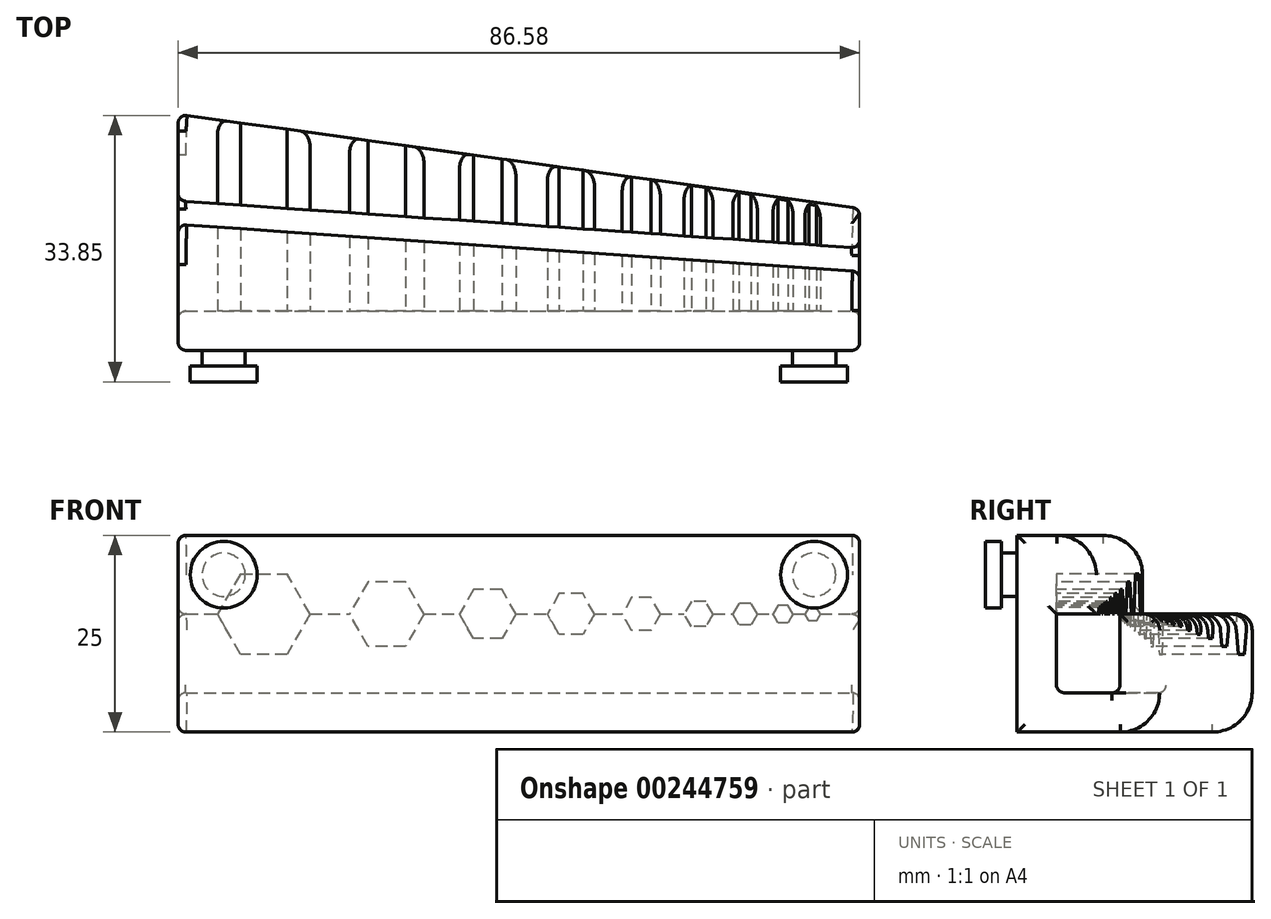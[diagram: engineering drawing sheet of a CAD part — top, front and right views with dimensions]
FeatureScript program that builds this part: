
annotation { "Feature Type Name" : "Feature", "Feature Type Description" : "" }
export const myFeature = defineFeature(function(context is Context, id is Id, definition is map)
    precondition{}
    {
        {
            var Q0;
            Q0=qCreatedBy(makeId("Front.planeOp"),FACE);
            var sketch = newSketch(context, id + "F0", { "sketchPlane" : qUnion([Q0])});
            skCircle(sketch, "E0.cCircle", {"center": v(-32.4, 0) * mm, "radius": 5.1 * mm, "construction": true});
            skLineSegment(sketch, "E0.0", {"start": v(-35.34, 5.1) * mm, "end": v(-29.45, 5.1) * mm});
            skLineSegment(sketch, "E0.1", {"start": v(-29.45, 5.1) * mm, "end": v(-26.5, 0) * mm});
            skLineSegment(sketch, "E0.2", {"start": v(-26.5, 0) * mm, "end": v(-29.45, -5.1) * mm});
            skLineSegment(sketch, "E0.3", {"start": v(-29.45, -5.1) * mm, "end": v(-35.34, -5.1) * mm});
            skLineSegment(sketch, "E0.4", {"start": v(-35.34, -5.1) * mm, "end": v(-38.29, 0) * mm});
            skLineSegment(sketch, "E0.5", {"start": v(-38.29, 0) * mm, "end": v(-35.34, 5.1) * mm});
            skPoint(sketch, "E0.0.midPoint", {"position": v(-32.4, 5.1) * mm});
            skCircle(sketch, "E1.cCircle", {"center": v(-16.78, 0) * mm, "radius": 4.1 * mm, "construction": true});
            skLineSegment(sketch, "E1.0", {"start": v(-14.4, -4.1) * mm, "end": v(-19.14, -4.1) * mm});
            skLineSegment(sketch, "E1.1", {"start": v(-19.14, -4.1) * mm, "end": v(-21.5, 0) * mm});
            skLineSegment(sketch, "E1.2", {"start": v(-21.5, 0) * mm, "end": v(-19.14, 4.1) * mm});
            skLineSegment(sketch, "E1.3", {"start": v(-19.14, 4.1) * mm, "end": v(-14.4, 4.1) * mm});
            skLineSegment(sketch, "E1.4", {"start": v(-14.4, 4.1) * mm, "end": v(-12.04, 0) * mm});
            skLineSegment(sketch, "E1.5", {"start": v(-12.04, 0) * mm, "end": v(-14.4, -4.1) * mm});
            skPoint(sketch, "E1.0.midPoint", {"position": v(-16.78, -4.1) * mm});
            skCircle(sketch, "E2.cCircle", {"center": v(-3.96, 0) * mm, "radius": 3.1 * mm, "construction": true});
            skLineSegment(sketch, "E2.0", {"start": v(-2.17, -3.1) * mm, "end": v(-5.75, -3.1) * mm});
            skLineSegment(sketch, "E2.1", {"start": v(-5.75, -3.1) * mm, "end": v(-7.54, 0) * mm});
            skLineSegment(sketch, "E2.2", {"start": v(-7.54, 0) * mm, "end": v(-5.75, 3.1) * mm});
            skLineSegment(sketch, "E2.3", {"start": v(-5.75, 3.1) * mm, "end": v(-2.17, 3.1) * mm});
            skLineSegment(sketch, "E2.4", {"start": v(-2.17, 3.1) * mm, "end": v(-0.38, 0) * mm});
            skLineSegment(sketch, "E2.5", {"start": v(-0.38, 0) * mm, "end": v(-2.17, -3.1) * mm});
            skPoint(sketch, "E2.0.midPoint", {"position": v(-3.96, -3.1) * mm});
            skCircle(sketch, "E3.cCircle", {"center": v(6.62, 0) * mm, "radius": 2.6 * mm, "construction": true});
            skLineSegment(sketch, "E3.0", {"start": v(8.12, -2.6) * mm, "end": v(5.12, -2.6) * mm});
            skLineSegment(sketch, "E3.1", {"start": v(5.12, -2.6) * mm, "end": v(3.62, 0) * mm});
            skLineSegment(sketch, "E3.2", {"start": v(3.62, 0) * mm, "end": v(5.12, 2.6) * mm});
            skLineSegment(sketch, "E3.3", {"start": v(5.12, 2.6) * mm, "end": v(8.12, 2.6) * mm});
            skLineSegment(sketch, "E3.4", {"start": v(8.12, 2.6) * mm, "end": v(9.62, 0) * mm});
            skLineSegment(sketch, "E3.5", {"start": v(9.62, 0) * mm, "end": v(8.12, -2.6) * mm});
            skPoint(sketch, "E3.0.midPoint", {"position": v(6.62, -2.6) * mm});
            skCircle(sketch, "E4.cCircle", {"center": v(15.55, 0) * mm, "radius": 2.1 * mm, "construction": true});
            skLineSegment(sketch, "E4.0", {"start": v(16.76, -2.1) * mm, "end": v(14.33, -2.1) * mm});
            skLineSegment(sketch, "E4.1", {"start": v(14.33, -2.1) * mm, "end": v(13.12, 0) * mm});
            skLineSegment(sketch, "E4.2", {"start": v(13.12, 0) * mm, "end": v(14.33, 2.1) * mm});
            skLineSegment(sketch, "E4.3", {"start": v(14.33, 2.1) * mm, "end": v(16.76, 2.1) * mm});
            skLineSegment(sketch, "E4.4", {"start": v(16.76, 2.1) * mm, "end": v(17.97, 0) * mm});
            skLineSegment(sketch, "E4.5", {"start": v(17.97, 0) * mm, "end": v(16.76, -2.1) * mm});
            skPoint(sketch, "E4.0.midPoint", {"position": v(15.55, -2.1) * mm});
            skCircle(sketch, "E5.cCircle", {"center": v(22.82, 0) * mm, "radius": 1.6 * mm, "construction": true});
            skLineSegment(sketch, "E5.0", {"start": v(23.74, -1.6) * mm, "end": v(21.9, -1.6) * mm});
            skLineSegment(sketch, "E5.1", {"start": v(21.9, -1.6) * mm, "end": v(20.97, 0) * mm});
            skLineSegment(sketch, "E5.2", {"start": v(20.97, 0) * mm, "end": v(21.9, 1.6) * mm});
            skLineSegment(sketch, "E5.3", {"start": v(21.9, 1.6) * mm, "end": v(23.74, 1.6) * mm});
            skLineSegment(sketch, "E5.4", {"start": v(23.74, 1.6) * mm, "end": v(24.67, 0) * mm});
            skLineSegment(sketch, "E5.5", {"start": v(24.67, 0) * mm, "end": v(23.74, -1.6) * mm});
            skPoint(sketch, "E5.0.midPoint", {"position": v(22.82, -1.6) * mm});
            skCircle(sketch, "E6.cCircle", {"center": v(28.73, 0) * mm, "radius": 1.35 * mm, "construction": true});
            skLineSegment(sketch, "E6.0", {"start": v(29.5, -1.35) * mm, "end": v(27.95, -1.35) * mm});
            skLineSegment(sketch, "E6.1", {"start": v(27.95, -1.35) * mm, "end": v(27.17, 0) * mm});
            skLineSegment(sketch, "E6.2", {"start": v(27.17, 0) * mm, "end": v(27.95, 1.35) * mm});
            skLineSegment(sketch, "E6.3", {"start": v(27.95, 1.35) * mm, "end": v(29.5, 1.35) * mm});
            skLineSegment(sketch, "E6.4", {"start": v(29.5, 1.35) * mm, "end": v(30.28, 0) * mm});
            skLineSegment(sketch, "E6.5", {"start": v(30.28, 0) * mm, "end": v(29.5, -1.35) * mm});
            skPoint(sketch, "E6.0.midPoint", {"position": v(28.73, -1.35) * mm});
            skCircle(sketch, "E7.cCircle", {"center": v(33.55, 0) * mm, "radius": 1.1 * mm, "construction": true});
            skLineSegment(sketch, "E7.0", {"start": v(34.19, -1.1) * mm, "end": v(32.92, -1.1) * mm});
            skLineSegment(sketch, "E7.1", {"start": v(32.92, -1.1) * mm, "end": v(32.28, 0) * mm});
            skLineSegment(sketch, "E7.2", {"start": v(32.28, 0) * mm, "end": v(32.92, 1.1) * mm});
            skLineSegment(sketch, "E7.3", {"start": v(32.92, 1.1) * mm, "end": v(34.19, 1.1) * mm});
            skLineSegment(sketch, "E7.4", {"start": v(34.19, 1.1) * mm, "end": v(34.82, 0) * mm});
            skLineSegment(sketch, "E7.5", {"start": v(34.82, 0) * mm, "end": v(34.19, -1.1) * mm});
            skPoint(sketch, "E7.0.midPoint", {"position": v(33.55, -1.1) * mm});
            skCircle(sketch, "E8.cCircle", {"center": v(37.3, 0) * mm, "radius": 0.85 * mm, "construction": true});
            skLineSegment(sketch, "E8.0", {"start": v(37.8, -0.85) * mm, "end": v(36.82, -0.85) * mm});
            skLineSegment(sketch, "E8.1", {"start": v(36.82, -0.85) * mm, "end": v(36.32, 0) * mm});
            skLineSegment(sketch, "E8.2", {"start": v(36.32, 0) * mm, "end": v(36.82, 0.85) * mm});
            skLineSegment(sketch, "E8.3", {"start": v(36.82, 0.85) * mm, "end": v(37.8, 0.85) * mm});
            skLineSegment(sketch, "E8.4", {"start": v(37.8, 0.85) * mm, "end": v(38.29, 0) * mm});
            skLineSegment(sketch, "E8.5", {"start": v(38.29, 0) * mm, "end": v(37.8, -0.85) * mm});
            skPoint(sketch, "E8.0.midPoint", {"position": v(37.3, -0.85) * mm});
            skLineSegment(sketch, "E9", {"start": v(38.29, -16.3) * mm, "end": v(-38.29, -16.3) * mm, "construction": true});
            skSolve(sketch);
        }
        {
            var Q0;
            Q0=qCreatedBy(makeId("Top.planeOp"),FACE);
            var sketch = newSketch(context, id + "F1", { "sketchPlane" : qUnion([Q0])});
            skLineSegment(sketch, "E10", {"start": v(-43.29, 0) * mm, "end": v(-43.29, 30) * mm});
            skLineSegment(sketch, "E11", {"start": v(-43.29, 30) * mm, "end": v(43.29, 18) * mm});
            skLineSegment(sketch, "E12", {"start": v(43.29, 18) * mm, "end": v(43.29, 0) * mm});
            skLineSegment(sketch, "E13", {"start": v(43.29, 0) * mm, "end": v(-43.29, 0) * mm});
            skLineSegment(sketch, "E14", {"start": v(-43.29, 17.5) * mm, "end": v(43.29, 11.5) * mm});
            skLineSegment(sketch, "E15", {"start": v(-43.29, 19) * mm, "end": v(43.29, 13) * mm});
            skLineSegment(sketch, "E16", {"start": v(-43.29, 16) * mm, "end": v(43.29, 10) * mm});
            skLineSegment(sketch, "E17", {"start": v(-43.29, 5) * mm, "end": v(43.29, 5) * mm});
            skPoint(sketch, "E18.0", {"position": v(-38.29, 0) * mm});
            skPoint(sketch, "E18.1", {"position": v(38.29, 0) * mm});
            skSolve(sketch);
        }
        {
            var Q0;
            {var subQ0=sQuery(id+"F1.wireOp",EDGE,"E16");Q0=makeQuery(id+"F1.imprint","IMPRINT",FACE,{"disambiguationData":[TD([[makeQuery(id+"F1.imprint","IMPRINT",EDGE,{"derivedFrom":subQ0}),-1.0]])]});}
            extrude(context, id + "F2", {"entities" : qUnion([Q0]), "depth" : 10 * mm});
        }
        {
            var Q0;
            {var subQ0=sQuery(id+"F1.wireOp",EDGE,"E16");Q0=makeQuery(id+"F1.imprint","IMPRINT",FACE,{"disambiguationData":[TD([[makeQuery(id+"F1.imprint","IMPRINT",EDGE,{"derivedFrom":subQ0}),-1.0]])]});}
            var Q1;
            {var subQ0=sQuery(id+"F1.wireOp",EDGE,"E11");Q1=makeQuery(id+"F1.imprint","IMPRINT",FACE,{"disambiguationData":[TD([[makeQuery(id+"F1.imprint","IMPRINT",EDGE,{"derivedFrom":subQ0}),-1.0]])]});}
            var Q2;
            {var subQ0=sQuery(id+"F1.wireOp",EDGE,"E14");Q2=makeQuery(id+"F1.imprint","IMPRINT",FACE,{"disambiguationData":[TD([[makeQuery(id+"F1.imprint","IMPRINT",EDGE,{"derivedFrom":subQ0}),-1.0]])]});}
            var Q3;
            {var subQ0=sQuery(id+"F1.wireOp",EDGE,"E14");Q3=makeQuery(id+"F1.imprint","IMPRINT",FACE,{"disambiguationData":[TD([[makeQuery(id+"F1.imprint","IMPRINT",EDGE,{"derivedFrom":subQ0}),1.0]])]});}
            extrude(context, id + "F3", {"entities" : qUnion([Q0, Q1, Q2, Q3]), "operationType" : NewBodyOperationType.ADD, "oppositeDirection" : true, "depth" : 15 * mm});
        }
        {
            var Q0;
            {var subQ0=sQuery(id+"F1.wireOp",EDGE,"E14");Q0=makeQuery(id+"F1.imprint","IMPRINT",FACE,{"disambiguationData":[TD([[makeQuery(id+"F1.imprint","IMPRINT",EDGE,{"derivedFrom":subQ0}),1.0]])]});}
            var Q1;
            {var subQ0=sQuery(id+"F1.wireOp",EDGE,"E14");Q1=makeQuery(id+"F1.imprint","IMPRINT",FACE,{"disambiguationData":[TD([[makeQuery(id+"F1.imprint","IMPRINT",EDGE,{"derivedFrom":subQ0}),-1.0]])]});}
            var Q2;
            {var subQ0=sQuery(id+"F1.wireOp",EDGE,"E16");Q2=makeQuery(id+"F1.imprint","IMPRINT",FACE,{"disambiguationData":[TD([[makeQuery(id+"F1.imprint","IMPRINT",EDGE,{"derivedFrom":subQ0}),-1.0]])]});}
            extrude(context, id + "F4", {"entities" : qUnion([Q0, Q1, Q2]), "operationType" : NewBodyOperationType.REMOVE, "oppositeDirection" : true, "depth" : 10 * mm});
        }
        {
            var Q0;
            Q0 = qSketchRegion(id + "F0", true);
            extrude(context, id + "F5", {"entities" : qUnion([Q0]), "operationType" : NewBodyOperationType.REMOVE, "endBound" : BoundingType.THROUGH_ALL, "oppositeDirection" : true, "depth" : 5 * mm});
        }
        {
            var Q0;
            {var subQ0=sQuery(id+"F1.wireOp",EDGE,"E13");Q0=makeQuery(id+"F1.imprint","IMPRINT",FACE,{"disambiguationData":[TD([[makeQuery(id+"F1.imprint","IMPRINT",EDGE,{"derivedFrom":subQ0}),-1.0]])]});}
            extrude(context, id + "F6", {"entities" : qUnion([Q0]), "operationType" : NewBodyOperationType.ADD, "depth" : 10 * mm, "hasSecondDirection" : true, "secondDirectionOppositeDirection" : true, "secondDirectionDepth" : 15 * mm});
        }
        {
            var Q0;
            Q0=makeQuery(id+"F2.opExtrude","CAP_EDGE",EDGE,{"disambiguationData":[OSD([sQuery(id+"F1.wireOp",EDGE,"E16")])],"isStart":false});
            var Q1;
            Q1=makeQuery(id+"F3.opExtrude","CAP_EDGE",EDGE,{"disambiguationData":[OSD([sQuery(id+"F1.wireOp",EDGE,"E11")])],"isStart":false});
            fillet(context, id + "F7", {"entities" : qUnion([Q0, Q1]), "radius" : 5 * mm, "tangentPropagation" : true, "allowEdgeOverflow" : false});
        }
        {
            var Q0;
            Q0=makeQuery(id+"F4.boolean.opBoolean","COPY",FACE,{"derivedFrom":makeQuery(id+"F4.opExtrude","CAP_FACE",FACE,{"disambiguationData":[OSD([sQuery(id+"F1.wireOp",EDGE,"E10"),sQuery(id+"F1.wireOp",EDGE,"E12"),sQuery(id+"F1.wireOp",EDGE,"E15"),sQuery(id+"F1.wireOp",EDGE,"E17")])],"isStart":false})});
            var Q1;
            {var subQ0=sQuery(id+"F1.wireOp",EDGE,"E12");var subQ1=sQuery(id+"F1.wireOp",EDGE,"E11");var subQ7=makeQuery(id+"F3.boolean.opBoolean","MERGE",FACE,{"derivedFrom":[makeQuery(id+"F2.opExtrude","SWEPT_FACE",FACE,{"disambiguationData":[OSD([subQ0])]}),makeQuery(id+"F3.opExtrude","SWEPT_FACE",FACE,{"disambiguationData":[OSD([subQ0])]})]});var subQ8=sQuery(id+"F1.wireOp",EDGE,"E16");Q1=makeQuery(id+"F6.boolean.opBoolean","MERGE",FACE,{"derivedFrom":[makeQuery(id+"F4.boolean.opBoolean","SPLIT",FACE,{"disambiguationData":[TD([makeQuery(id+"F2.opExtrude","SWEPT_FACE",FACE,{"disambiguationData":[OSD([subQ8])]})])],"derivedFrom":subQ7}),makeQuery(id+"F4.boolean.opBoolean","SPLIT",FACE,{"disambiguationData":[TD([makeQuery(id+"F3.opExtrude","SWEPT_FACE",FACE,{"disambiguationData":[OSD([subQ1])]})])],"derivedFrom":subQ7}),makeQuery(id+"F6.opExtrude","SWEPT_FACE",FACE,{"disambiguationData":[OSD([subQ0])]})]});}
            var Q2;
            {var subQ0=sQuery(id+"F1.wireOp",EDGE,"E10");var subQ1=sQuery(id+"F1.wireOp",EDGE,"E11");var subQ7=makeQuery(id+"F3.boolean.opBoolean","MERGE",FACE,{"derivedFrom":[makeQuery(id+"F2.opExtrude","SWEPT_FACE",FACE,{"disambiguationData":[OSD([subQ0])]}),makeQuery(id+"F3.opExtrude","SWEPT_FACE",FACE,{"disambiguationData":[OSD([subQ0])]})]});var subQ8=sQuery(id+"F1.wireOp",EDGE,"E16");Q2=makeQuery(id+"F6.boolean.opBoolean","MERGE",FACE,{"derivedFrom":[makeQuery(id+"F4.boolean.opBoolean","SPLIT",FACE,{"disambiguationData":[TD([makeQuery(id+"F2.opExtrude","SWEPT_FACE",FACE,{"disambiguationData":[OSD([subQ8])]})])],"derivedFrom":subQ7}),makeQuery(id+"F4.boolean.opBoolean","SPLIT",FACE,{"disambiguationData":[TD([makeQuery(id+"F3.opExtrude","SWEPT_FACE",FACE,{"disambiguationData":[OSD([subQ1])]})])],"derivedFrom":subQ7}),makeQuery(id+"F6.opExtrude","SWEPT_FACE",FACE,{"disambiguationData":[OSD([subQ0])]})]});}
            fillet(context, id + "F8", {"entities" : qUnion([Q0, Q1, Q2]), "radius" : 1 * mm, "tangentPropagation" : true, "allowEdgeOverflow" : false});
        }
        {
            var Q0;
            {var subQ0=sQuery(id+"F1.wireOp",EDGE,"E11");var subQ1=sQuery(id+"F1.wireOp",EDGE,"E10");Q0=makeQuery(id+"F5.boolean.opBoolean","SPLIT",EDGE,{"disambiguationData":[TD([makeQuery(id+"F2.opExtrude","SWEPT_FACE",FACE,{"disambiguationData":[OSD([subQ1])]})])],"derivedFrom":makeQuery(id+"F3.opExtrude","CAP_EDGE",EDGE,{"disambiguationData":[OSD([subQ0])],"isStart":true})});}
            var Q1;
            {var subQ0=sQuery(id+"F1.wireOp",EDGE,"E11");Q1=makeQuery(id+"F5.boolean.opBoolean","SPLIT",EDGE,{"disambiguationData":[TD([makeQuery(id+"F5.opExtrude","SWEPT_FACE",FACE,{"disambiguationData":[OSD([sQuery(id+"F0.wireOp",EDGE,"E0.2")])]})])],"derivedFrom":makeQuery(id+"F3.opExtrude","CAP_EDGE",EDGE,{"disambiguationData":[OSD([subQ0])],"isStart":true})});}
            var Q2;
            {var subQ0=sQuery(id+"F1.wireOp",EDGE,"E10");var subQ1=sQuery(id+"F1.wireOp",EDGE,"E16");Q2=makeQuery(id+"F5.boolean.opBoolean","SPLIT",EDGE,{"disambiguationData":[TD([makeQuery(id+"F2.opExtrude","SWEPT_FACE",FACE,{"disambiguationData":[OSD([subQ0])]})])],"derivedFrom":makeQuery(id+"F2.opExtrude","CAP_EDGE",EDGE,{"disambiguationData":[OSD([subQ1])],"isStart":true})});}
            var Q3;
            {var subQ0=sQuery(id+"F1.wireOp",EDGE,"E16");Q3=makeQuery(id+"F5.boolean.opBoolean","SPLIT",EDGE,{"disambiguationData":[TD([makeQuery(id+"F5.opExtrude","SWEPT_FACE",FACE,{"disambiguationData":[OSD([sQuery(id+"F0.wireOp",EDGE,"E0.1")])]})])],"derivedFrom":makeQuery(id+"F2.opExtrude","CAP_EDGE",EDGE,{"disambiguationData":[OSD([subQ0])],"isStart":true})});}
            var Q4;
            {var subQ0=sQuery(id+"F1.wireOp",EDGE,"E11");Q4=makeQuery(id+"F5.boolean.opBoolean","SPLIT",EDGE,{"disambiguationData":[TD([makeQuery(id+"F5.opExtrude","SWEPT_FACE",FACE,{"disambiguationData":[OSD([sQuery(id+"F0.wireOp",EDGE,"E1.5")])]})])],"derivedFrom":makeQuery(id+"F3.opExtrude","CAP_EDGE",EDGE,{"disambiguationData":[OSD([subQ0])],"isStart":true})});}
            var Q5;
            {var subQ0=sQuery(id+"F1.wireOp",EDGE,"E11");Q5=makeQuery(id+"F5.boolean.opBoolean","SPLIT",EDGE,{"disambiguationData":[TD([makeQuery(id+"F5.opExtrude","SWEPT_FACE",FACE,{"disambiguationData":[OSD([sQuery(id+"F0.wireOp",EDGE,"E2.5")])]})])],"derivedFrom":makeQuery(id+"F3.opExtrude","CAP_EDGE",EDGE,{"disambiguationData":[OSD([subQ0])],"isStart":true})});}
            var Q6;
            {var subQ0=sQuery(id+"F1.wireOp",EDGE,"E11");Q6=makeQuery(id+"F5.boolean.opBoolean","SPLIT",EDGE,{"disambiguationData":[TD([makeQuery(id+"F5.opExtrude","SWEPT_FACE",FACE,{"disambiguationData":[OSD([sQuery(id+"F0.wireOp",EDGE,"E3.5")])]})])],"derivedFrom":makeQuery(id+"F3.opExtrude","CAP_EDGE",EDGE,{"disambiguationData":[OSD([subQ0])],"isStart":true})});}
            var Q7;
            {var subQ0=sQuery(id+"F1.wireOp",EDGE,"E11");Q7=makeQuery(id+"F5.boolean.opBoolean","SPLIT",EDGE,{"disambiguationData":[TD([makeQuery(id+"F5.opExtrude","SWEPT_FACE",FACE,{"disambiguationData":[OSD([sQuery(id+"F0.wireOp",EDGE,"E4.5")])]})])],"derivedFrom":makeQuery(id+"F3.opExtrude","CAP_EDGE",EDGE,{"disambiguationData":[OSD([subQ0])],"isStart":true})});}
            var Q8;
            {var subQ0=sQuery(id+"F1.wireOp",EDGE,"E11");Q8=makeQuery(id+"F5.boolean.opBoolean","SPLIT",EDGE,{"disambiguationData":[TD([makeQuery(id+"F5.opExtrude","SWEPT_FACE",FACE,{"disambiguationData":[OSD([sQuery(id+"F0.wireOp",EDGE,"E5.5")])]})])],"derivedFrom":makeQuery(id+"F3.opExtrude","CAP_EDGE",EDGE,{"disambiguationData":[OSD([subQ0])],"isStart":true})});}
            var Q9;
            {var subQ0=sQuery(id+"F1.wireOp",EDGE,"E16");Q9=makeQuery(id+"F5.boolean.opBoolean","SPLIT",EDGE,{"disambiguationData":[TD([makeQuery(id+"F5.opExtrude","SWEPT_FACE",FACE,{"disambiguationData":[OSD([sQuery(id+"F0.wireOp",EDGE,"E1.4")])]})])],"derivedFrom":makeQuery(id+"F2.opExtrude","CAP_EDGE",EDGE,{"disambiguationData":[OSD([subQ0])],"isStart":true})});}
            var Q10;
            {var subQ0=sQuery(id+"F1.wireOp",EDGE,"E16");Q10=makeQuery(id+"F5.boolean.opBoolean","SPLIT",EDGE,{"disambiguationData":[TD([makeQuery(id+"F5.opExtrude","SWEPT_FACE",FACE,{"disambiguationData":[OSD([sQuery(id+"F0.wireOp",EDGE,"E2.4")])]})])],"derivedFrom":makeQuery(id+"F2.opExtrude","CAP_EDGE",EDGE,{"disambiguationData":[OSD([subQ0])],"isStart":true})});}
            var Q11;
            {var subQ0=sQuery(id+"F1.wireOp",EDGE,"E16");Q11=makeQuery(id+"F5.boolean.opBoolean","SPLIT",EDGE,{"disambiguationData":[TD([makeQuery(id+"F5.opExtrude","SWEPT_FACE",FACE,{"disambiguationData":[OSD([sQuery(id+"F0.wireOp",EDGE,"E3.4")])]})])],"derivedFrom":makeQuery(id+"F2.opExtrude","CAP_EDGE",EDGE,{"disambiguationData":[OSD([subQ0])],"isStart":true})});}
            var Q12;
            {var subQ0=sQuery(id+"F1.wireOp",EDGE,"E16");Q12=makeQuery(id+"F5.boolean.opBoolean","SPLIT",EDGE,{"disambiguationData":[TD([makeQuery(id+"F5.opExtrude","SWEPT_FACE",FACE,{"disambiguationData":[OSD([sQuery(id+"F0.wireOp",EDGE,"E4.4")])]})])],"derivedFrom":makeQuery(id+"F2.opExtrude","CAP_EDGE",EDGE,{"disambiguationData":[OSD([subQ0])],"isStart":true})});}
            var Q13;
            {var subQ0=sQuery(id+"F1.wireOp",EDGE,"E16");Q13=makeQuery(id+"F5.boolean.opBoolean","SPLIT",EDGE,{"disambiguationData":[TD([makeQuery(id+"F5.opExtrude","SWEPT_FACE",FACE,{"disambiguationData":[OSD([sQuery(id+"F0.wireOp",EDGE,"E5.4")])]})])],"derivedFrom":makeQuery(id+"F2.opExtrude","CAP_EDGE",EDGE,{"disambiguationData":[OSD([subQ0])],"isStart":true})});}
            fillet(context, id + "F9", {"entities" : qUnion([Q0, Q1, Q2, Q3, Q4, Q5, Q6, Q7, Q8, Q9, Q10, Q11, Q12, Q13]), "radius" : 2 * mm, "tangentPropagation" : true, "allowEdgeOverflow" : false});
        }
        {
            var Q0;
            Q0=makeQuery(id+"F6.opExtrude","SWEPT_FACE",FACE,{"disambiguationData":[OSD([sQuery(id+"F1.wireOp",EDGE,"E13")])]});
            var sketch = newSketch(context, id + "F10", { "sketchPlane" : qUnion([Q0])});
            skPoint(sketch, "E19", {"position": v(-37.5, 5) * mm});
            skPoint(sketch, "E20", {"position": v(37.5, 5) * mm});
            skCircle(sketch, "E21", {"center": v(-37.5, 5) * mm, "radius": 2.75 * mm});
            skCircle(sketch, "E22", {"center": v(37.5, 5) * mm, "radius": 2.75 * mm});
            skSolve(sketch);
        }
        {
            var Q0;
            Q0 = qSketchRegion(id + "F10", true);
            extrude(context, id + "F11", {"entities" : qUnion([Q0]), "operationType" : NewBodyOperationType.ADD, "depth" : 2 * mm});
        }
        {
            var Q0;
            Q0=makeQuery(id+"F11.opExtrude","CAP_FACE",FACE,{"disambiguationData":[OSD([sQuery(id+"F10.wireOp",EDGE,"E21")])],"isStart":false});
            var sketch = newSketch(context, id + "F12", { "sketchPlane" : qUnion([Q0])});
            skCircle(sketch, "E23", {"center": v(-37.5, 5) * mm, "radius": 4.25 * mm});
            skCircle(sketch, "E24.0.0", {"center": v(37.5, 5) * mm, "radius": 2.75 * mm, "construction": true});
            skCircle(sketch, "E25", {"center": v(37.5, 5) * mm, "radius": 4.25 * mm});
            skSolve(sketch);
        }
        {
            var Q0;
            Q0 = qSketchRegion(id + "F12", true);
            extrude(context, id + "F13", {"entities" : qUnion([Q0]), "operationType" : NewBodyOperationType.ADD, "depth" : 2 * mm});
        }
    });
